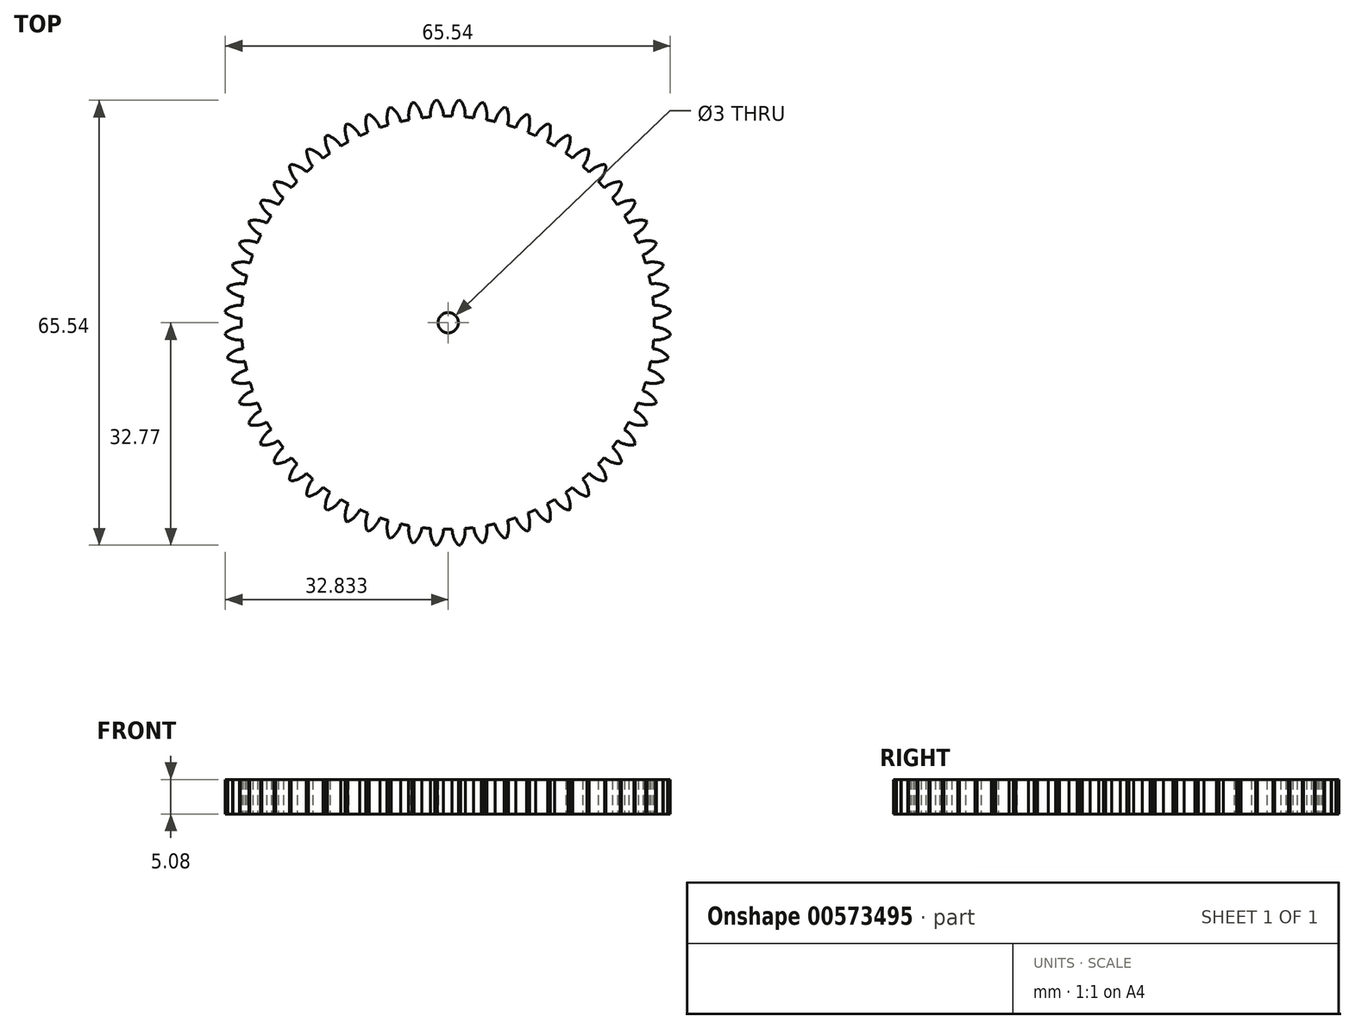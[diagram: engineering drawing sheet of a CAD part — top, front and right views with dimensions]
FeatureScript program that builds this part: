
annotation { "Feature Type Name" : "Feature", "Feature Type Description" : "" }
export const myFeature = defineFeature(function(context is Context, id is Id, definition is map)
    precondition{}
    {
        {
            var Q0;
            Q0=qCreatedBy(makeId("Top.planeOp"),FACE);
            var sketch = newSketch(context, id + "F0", { "sketchPlane" : qUnion([Q0])});
            skArc(sketch, "E0", {"start": v(-17.72, -27.6) * mm, "mid": v(-16.6, -26.98) * mm, "end": v(-15.76, -26.02) * mm});
            skLineSegment(sketch, "E1", {"start": v(-17.72, -27.6) * mm, "end": v(-18.01, -27.42) * mm});
            skArc(sketch, "E2", {"start": v(-17.36, -24.98) * mm, "mid": v(-17.9, -26.14) * mm, "end": v(-18.01, -27.42) * mm});
            skArc(sketch, "E3", {"start": v(-18.4, -24.23) * mm, "mid": v(-17.88, -24.6) * mm, "end": v(-17.36, -24.98) * mm});
            skArc(sketch, "E4.1.0", {"start": v(-14.74, -29.3) * mm, "mid": v(-13.69, -28.57) * mm, "end": v(-12.95, -27.52) * mm});
            skLineSegment(sketch, "E4.1.1", {"start": v(-14.74, -29.3) * mm, "end": v(-15.05, -29.15) * mm});
            skArc(sketch, "E4.1.2", {"start": v(-14.65, -26.66) * mm, "mid": v(-15.07, -27.87) * mm, "end": v(-15.05, -29.15) * mm});
            skArc(sketch, "E4.1.3", {"start": v(-15.76, -26.02) * mm, "mid": v(-15.2, -26.34) * mm, "end": v(-14.65, -26.66) * mm});
            skArc(sketch, "E4.2.0", {"start": v(-11.6, -30.69) * mm, "mid": v(-10.63, -29.85) * mm, "end": v(-10, -28.73) * mm});
            skLineSegment(sketch, "E4.2.1", {"start": v(-11.6, -30.69) * mm, "end": v(-11.92, -30.56) * mm});
            skArc(sketch, "E4.2.2", {"start": v(-11.79, -28.04) * mm, "mid": v(-12.07, -29.3) * mm, "end": v(-11.92, -30.56) * mm});
            skArc(sketch, "E4.2.3", {"start": v(-12.95, -27.52) * mm, "mid": v(-12.37, -27.79) * mm, "end": v(-11.79, -28.04) * mm});
            skArc(sketch, "E4.3.0", {"start": v(-8.32, -31.73) * mm, "mid": v(-7.45, -30.8) * mm, "end": v(-6.95, -29.61) * mm});
            skLineSegment(sketch, "E4.3.1", {"start": v(-8.32, -31.73) * mm, "end": v(-8.66, -31.64) * mm});
            skArc(sketch, "E4.3.2", {"start": v(-8.8, -29.12) * mm, "mid": v(-8.94, -30.4) * mm, "end": v(-8.66, -31.64) * mm});
            skArc(sketch, "E4.3.3", {"start": v(-10, -28.73) * mm, "mid": v(-9.4, -28.93) * mm, "end": v(-8.8, -29.12) * mm});
            skArc(sketch, "E4.4.0", {"start": v(-4.96, -32.43) * mm, "mid": v(-4.2, -31.4) * mm, "end": v(-3.81, -30.18) * mm});
            skLineSegment(sketch, "E4.4.1", {"start": v(-4.96, -32.43) * mm, "end": v(-5.3, -32.37) * mm});
            skArc(sketch, "E4.4.2", {"start": v(-5.7, -29.88) * mm, "mid": v(-5.72, -31.16) * mm, "end": v(-5.3, -32.37) * mm});
            skArc(sketch, "E4.4.3", {"start": v(-6.95, -29.61) * mm, "mid": v(-6.32, -29.75) * mm, "end": v(-5.7, -29.88) * mm});
            skArc(sketch, "E4.5.0", {"start": v(-1.55, -32.77) * mm, "mid": v(-0.88, -31.67) * mm, "end": v(-0.64, -30.41) * mm});
            skLineSegment(sketch, "E4.5.1", {"start": v(-1.55, -32.77) * mm, "end": v(-1.89, -32.75) * mm});
            skArc(sketch, "E4.5.2", {"start": v(-2.55, -30.31) * mm, "mid": v(-2.43, -31.59) * mm, "end": v(-1.89, -32.75) * mm});
            skArc(sketch, "E4.5.3", {"start": v(-3.81, -30.18) * mm, "mid": v(-3.18, -30.25) * mm, "end": v(-2.55, -30.31) * mm});
            skArc(sketch, "E4.6.0", {"start": v(1.89, -32.75) * mm, "mid": v(2.43, -31.59) * mm, "end": v(2.55, -30.31) * mm});
            skLineSegment(sketch, "E4.6.1", {"start": v(1.89, -32.75) * mm, "end": v(1.55, -32.77) * mm});
            skArc(sketch, "E4.6.2", {"start": v(0.64, -30.41) * mm, "mid": v(0.88, -31.67) * mm, "end": v(1.55, -32.77) * mm});
            skArc(sketch, "E4.6.3", {"start": v(-0.64, -30.41) * mm, "mid": v(0, -30.42) * mm, "end": v(0.64, -30.41) * mm});
            skArc(sketch, "E4.7.0", {"start": v(5.3, -32.37) * mm, "mid": v(5.72, -31.16) * mm, "end": v(5.7, -29.88) * mm});
            skLineSegment(sketch, "E4.7.1", {"start": v(5.3, -32.37) * mm, "end": v(4.96, -32.43) * mm});
            skArc(sketch, "E4.7.2", {"start": v(3.81, -30.18) * mm, "mid": v(4.2, -31.4) * mm, "end": v(4.96, -32.43) * mm});
            skArc(sketch, "E4.7.3", {"start": v(2.55, -30.31) * mm, "mid": v(3.18, -30.25) * mm, "end": v(3.81, -30.18) * mm});
            skArc(sketch, "E4.8.0", {"start": v(8.66, -31.64) * mm, "mid": v(8.94, -30.4) * mm, "end": v(8.8, -29.12) * mm});
            skLineSegment(sketch, "E4.8.1", {"start": v(8.66, -31.64) * mm, "end": v(8.32, -31.73) * mm});
            skArc(sketch, "E4.8.2", {"start": v(6.95, -29.61) * mm, "mid": v(7.45, -30.8) * mm, "end": v(8.32, -31.73) * mm});
            skArc(sketch, "E4.8.3", {"start": v(5.7, -29.88) * mm, "mid": v(6.32, -29.75) * mm, "end": v(6.95, -29.61) * mm});
            skArc(sketch, "E4.9.0", {"start": v(11.92, -30.56) * mm, "mid": v(12.07, -29.3) * mm, "end": v(11.79, -28.04) * mm});
            skLineSegment(sketch, "E4.9.1", {"start": v(11.92, -30.56) * mm, "end": v(11.6, -30.69) * mm});
            skArc(sketch, "E4.9.2", {"start": v(10, -28.73) * mm, "mid": v(10.63, -29.85) * mm, "end": v(11.6, -30.69) * mm});
            skArc(sketch, "E4.9.3", {"start": v(8.8, -29.12) * mm, "mid": v(9.4, -28.93) * mm, "end": v(10, -28.73) * mm});
            skArc(sketch, "E4.10.0", {"start": v(15.05, -29.15) * mm, "mid": v(15.07, -27.87) * mm, "end": v(14.65, -26.66) * mm});
            skLineSegment(sketch, "E4.10.1", {"start": v(15.05, -29.15) * mm, "end": v(14.74, -29.3) * mm});
            skArc(sketch, "E4.10.2", {"start": v(12.95, -27.52) * mm, "mid": v(13.69, -28.57) * mm, "end": v(14.74, -29.3) * mm});
            skArc(sketch, "E4.10.3", {"start": v(11.79, -28.04) * mm, "mid": v(12.37, -27.79) * mm, "end": v(12.95, -27.52) * mm});
            skArc(sketch, "E4.11.0", {"start": v(18.01, -27.42) * mm, "mid": v(17.9, -26.14) * mm, "end": v(17.36, -24.98) * mm});
            skLineSegment(sketch, "E4.11.1", {"start": v(18.01, -27.42) * mm, "end": v(17.72, -27.6) * mm});
            skArc(sketch, "E4.11.2", {"start": v(15.76, -26.02) * mm, "mid": v(16.6, -26.98) * mm, "end": v(17.72, -27.6) * mm});
            skArc(sketch, "E4.11.3", {"start": v(14.65, -26.66) * mm, "mid": v(15.2, -26.34) * mm, "end": v(15.76, -26.02) * mm});
            skArc(sketch, "E4.12.0", {"start": v(20.78, -25.39) * mm, "mid": v(20.53, -24.13) * mm, "end": v(19.88, -23.03) * mm});
            skLineSegment(sketch, "E4.12.1", {"start": v(20.78, -25.39) * mm, "end": v(20.51, -25.6) * mm});
            skArc(sketch, "E4.12.2", {"start": v(18.4, -24.23) * mm, "mid": v(19.33, -25.1) * mm, "end": v(20.51, -25.6) * mm});
            skArc(sketch, "E4.12.3", {"start": v(17.36, -24.98) * mm, "mid": v(17.88, -24.6) * mm, "end": v(18.4, -24.23) * mm});
            skArc(sketch, "E4.13.0", {"start": v(23.32, -23.07) * mm, "mid": v(22.94, -21.85) * mm, "end": v(22.17, -20.82) * mm});
            skLineSegment(sketch, "E4.13.1", {"start": v(23.32, -23.07) * mm, "end": v(23.07, -23.32) * mm});
            skArc(sketch, "E4.13.2", {"start": v(20.82, -22.17) * mm, "mid": v(21.85, -22.94) * mm, "end": v(23.07, -23.32) * mm});
            skArc(sketch, "E4.13.3", {"start": v(19.88, -23.03) * mm, "mid": v(20.35, -22.6) * mm, "end": v(20.82, -22.17) * mm});
            skArc(sketch, "E4.14.0", {"start": v(25.6, -20.51) * mm, "mid": v(25.1, -19.33) * mm, "end": v(24.23, -18.4) * mm});
            skLineSegment(sketch, "E4.14.1", {"start": v(25.6, -20.51) * mm, "end": v(25.39, -20.78) * mm});
            skArc(sketch, "E4.14.2", {"start": v(23.03, -19.88) * mm, "mid": v(24.13, -20.53) * mm, "end": v(25.39, -20.78) * mm});
            skArc(sketch, "E4.14.3", {"start": v(22.17, -20.82) * mm, "mid": v(22.6, -20.35) * mm, "end": v(23.03, -19.88) * mm});
            skArc(sketch, "E4.15.0", {"start": v(27.6, -17.72) * mm, "mid": v(26.98, -16.6) * mm, "end": v(26.02, -15.76) * mm});
            skLineSegment(sketch, "E4.15.1", {"start": v(27.6, -17.72) * mm, "end": v(27.42, -18.01) * mm});
            skArc(sketch, "E4.15.2", {"start": v(24.98, -17.36) * mm, "mid": v(26.14, -17.9) * mm, "end": v(27.42, -18.01) * mm});
            skArc(sketch, "E4.15.3", {"start": v(24.23, -18.4) * mm, "mid": v(24.6, -17.88) * mm, "end": v(24.98, -17.36) * mm});
            skArc(sketch, "E4.16.0", {"start": v(29.3, -14.74) * mm, "mid": v(28.57, -13.69) * mm, "end": v(27.52, -12.95) * mm});
            skLineSegment(sketch, "E4.16.1", {"start": v(29.3, -14.74) * mm, "end": v(29.15, -15.05) * mm});
            skArc(sketch, "E4.16.2", {"start": v(26.66, -14.65) * mm, "mid": v(27.87, -15.07) * mm, "end": v(29.15, -15.05) * mm});
            skArc(sketch, "E4.16.3", {"start": v(26.02, -15.76) * mm, "mid": v(26.34, -15.2) * mm, "end": v(26.66, -14.65) * mm});
            skArc(sketch, "E4.17.0", {"start": v(30.69, -11.6) * mm, "mid": v(29.85, -10.63) * mm, "end": v(28.73, -10) * mm});
            skLineSegment(sketch, "E4.17.1", {"start": v(30.69, -11.6) * mm, "end": v(30.56, -11.92) * mm});
            skArc(sketch, "E4.17.2", {"start": v(28.04, -11.79) * mm, "mid": v(29.3, -12.07) * mm, "end": v(30.56, -11.92) * mm});
            skArc(sketch, "E4.17.3", {"start": v(27.52, -12.95) * mm, "mid": v(27.79, -12.37) * mm, "end": v(28.04, -11.79) * mm});
            skArc(sketch, "E4.18.0", {"start": v(31.73, -8.32) * mm, "mid": v(30.8, -7.45) * mm, "end": v(29.61, -6.95) * mm});
            skLineSegment(sketch, "E4.18.1", {"start": v(31.73, -8.32) * mm, "end": v(31.64, -8.66) * mm});
            skArc(sketch, "E4.18.2", {"start": v(29.12, -8.8) * mm, "mid": v(30.4, -8.94) * mm, "end": v(31.64, -8.66) * mm});
            skArc(sketch, "E4.18.3", {"start": v(28.73, -10) * mm, "mid": v(28.93, -9.4) * mm, "end": v(29.12, -8.8) * mm});
            skArc(sketch, "E4.19.0", {"start": v(32.43, -4.96) * mm, "mid": v(31.4, -4.2) * mm, "end": v(30.18, -3.81) * mm});
            skLineSegment(sketch, "E4.19.1", {"start": v(32.43, -4.96) * mm, "end": v(32.37, -5.3) * mm});
            skArc(sketch, "E4.19.2", {"start": v(29.88, -5.7) * mm, "mid": v(31.16, -5.72) * mm, "end": v(32.37, -5.3) * mm});
            skArc(sketch, "E4.19.3", {"start": v(29.61, -6.95) * mm, "mid": v(29.75, -6.32) * mm, "end": v(29.88, -5.7) * mm});
            skArc(sketch, "E4.20.0", {"start": v(32.77, -1.55) * mm, "mid": v(31.67, -0.88) * mm, "end": v(30.41, -0.64) * mm});
            skLineSegment(sketch, "E4.20.1", {"start": v(32.77, -1.55) * mm, "end": v(32.75, -1.89) * mm});
            skArc(sketch, "E4.20.2", {"start": v(30.31, -2.55) * mm, "mid": v(31.59, -2.43) * mm, "end": v(32.75, -1.89) * mm});
            skArc(sketch, "E4.20.3", {"start": v(30.18, -3.81) * mm, "mid": v(30.25, -3.18) * mm, "end": v(30.31, -2.55) * mm});
            skArc(sketch, "E4.21.0", {"start": v(32.75, 1.89) * mm, "mid": v(31.59, 2.43) * mm, "end": v(30.31, 2.55) * mm});
            skLineSegment(sketch, "E4.21.1", {"start": v(32.75, 1.89) * mm, "end": v(32.77, 1.55) * mm});
            skArc(sketch, "E4.21.2", {"start": v(30.41, 0.64) * mm, "mid": v(31.67, 0.88) * mm, "end": v(32.77, 1.55) * mm});
            skArc(sketch, "E4.21.3", {"start": v(30.41, -0.64) * mm, "mid": v(30.42, 0) * mm, "end": v(30.41, 0.64) * mm});
            skArc(sketch, "E4.22.0", {"start": v(32.37, 5.3) * mm, "mid": v(31.16, 5.72) * mm, "end": v(29.88, 5.7) * mm});
            skLineSegment(sketch, "E4.22.1", {"start": v(32.37, 5.3) * mm, "end": v(32.43, 4.96) * mm});
            skArc(sketch, "E4.22.2", {"start": v(30.18, 3.81) * mm, "mid": v(31.4, 4.2) * mm, "end": v(32.43, 4.96) * mm});
            skArc(sketch, "E4.22.3", {"start": v(30.31, 2.55) * mm, "mid": v(30.25, 3.18) * mm, "end": v(30.18, 3.81) * mm});
            skArc(sketch, "E4.23.0", {"start": v(31.64, 8.66) * mm, "mid": v(30.4, 8.94) * mm, "end": v(29.12, 8.8) * mm});
            skLineSegment(sketch, "E4.23.1", {"start": v(31.64, 8.66) * mm, "end": v(31.73, 8.32) * mm});
            skArc(sketch, "E4.23.2", {"start": v(29.61, 6.95) * mm, "mid": v(30.8, 7.45) * mm, "end": v(31.73, 8.32) * mm});
            skArc(sketch, "E4.23.3", {"start": v(29.88, 5.7) * mm, "mid": v(29.75, 6.32) * mm, "end": v(29.61, 6.95) * mm});
            skArc(sketch, "E4.24.0", {"start": v(30.56, 11.92) * mm, "mid": v(29.3, 12.07) * mm, "end": v(28.04, 11.79) * mm});
            skLineSegment(sketch, "E4.24.1", {"start": v(30.56, 11.92) * mm, "end": v(30.69, 11.6) * mm});
            skArc(sketch, "E4.24.2", {"start": v(28.73, 10) * mm, "mid": v(29.85, 10.63) * mm, "end": v(30.69, 11.6) * mm});
            skArc(sketch, "E4.24.3", {"start": v(29.12, 8.8) * mm, "mid": v(28.93, 9.4) * mm, "end": v(28.73, 10) * mm});
            skArc(sketch, "E4.25.0", {"start": v(29.15, 15.05) * mm, "mid": v(27.87, 15.07) * mm, "end": v(26.66, 14.65) * mm});
            skLineSegment(sketch, "E4.25.1", {"start": v(29.15, 15.05) * mm, "end": v(29.3, 14.74) * mm});
            skArc(sketch, "E4.25.2", {"start": v(27.52, 12.95) * mm, "mid": v(28.57, 13.69) * mm, "end": v(29.3, 14.74) * mm});
            skArc(sketch, "E4.25.3", {"start": v(28.04, 11.79) * mm, "mid": v(27.79, 12.37) * mm, "end": v(27.52, 12.95) * mm});
            skArc(sketch, "E4.26.0", {"start": v(27.42, 18.01) * mm, "mid": v(26.14, 17.9) * mm, "end": v(24.98, 17.36) * mm});
            skLineSegment(sketch, "E4.26.1", {"start": v(27.42, 18.01) * mm, "end": v(27.6, 17.72) * mm});
            skArc(sketch, "E4.26.2", {"start": v(26.02, 15.76) * mm, "mid": v(26.98, 16.6) * mm, "end": v(27.6, 17.72) * mm});
            skArc(sketch, "E4.26.3", {"start": v(26.66, 14.65) * mm, "mid": v(26.34, 15.2) * mm, "end": v(26.02, 15.76) * mm});
            skArc(sketch, "E4.27.0", {"start": v(25.39, 20.78) * mm, "mid": v(24.13, 20.53) * mm, "end": v(23.03, 19.88) * mm});
            skLineSegment(sketch, "E4.27.1", {"start": v(25.39, 20.78) * mm, "end": v(25.6, 20.51) * mm});
            skArc(sketch, "E4.27.2", {"start": v(24.23, 18.4) * mm, "mid": v(25.1, 19.33) * mm, "end": v(25.6, 20.51) * mm});
            skArc(sketch, "E4.27.3", {"start": v(24.98, 17.36) * mm, "mid": v(24.6, 17.88) * mm, "end": v(24.23, 18.4) * mm});
            skArc(sketch, "E4.28.0", {"start": v(23.07, 23.32) * mm, "mid": v(21.85, 22.94) * mm, "end": v(20.82, 22.17) * mm});
            skLineSegment(sketch, "E4.28.1", {"start": v(23.07, 23.32) * mm, "end": v(23.32, 23.07) * mm});
            skArc(sketch, "E4.28.2", {"start": v(22.17, 20.82) * mm, "mid": v(22.94, 21.85) * mm, "end": v(23.32, 23.07) * mm});
            skArc(sketch, "E4.28.3", {"start": v(23.03, 19.88) * mm, "mid": v(22.6, 20.35) * mm, "end": v(22.17, 20.82) * mm});
            skArc(sketch, "E4.29.0", {"start": v(20.51, 25.6) * mm, "mid": v(19.33, 25.1) * mm, "end": v(18.4, 24.23) * mm});
            skLineSegment(sketch, "E4.29.1", {"start": v(20.51, 25.6) * mm, "end": v(20.78, 25.39) * mm});
            skArc(sketch, "E4.29.2", {"start": v(19.88, 23.03) * mm, "mid": v(20.53, 24.13) * mm, "end": v(20.78, 25.39) * mm});
            skArc(sketch, "E4.29.3", {"start": v(20.82, 22.17) * mm, "mid": v(20.35, 22.6) * mm, "end": v(19.88, 23.03) * mm});
            skArc(sketch, "E4.30.0", {"start": v(17.72, 27.6) * mm, "mid": v(16.6, 26.98) * mm, "end": v(15.76, 26.02) * mm});
            skLineSegment(sketch, "E4.30.1", {"start": v(17.72, 27.6) * mm, "end": v(18.01, 27.42) * mm});
            skArc(sketch, "E4.30.2", {"start": v(17.36, 24.98) * mm, "mid": v(17.9, 26.14) * mm, "end": v(18.01, 27.42) * mm});
            skArc(sketch, "E4.30.3", {"start": v(18.4, 24.23) * mm, "mid": v(17.88, 24.6) * mm, "end": v(17.36, 24.98) * mm});
            skArc(sketch, "E4.31.0", {"start": v(14.74, 29.3) * mm, "mid": v(13.69, 28.57) * mm, "end": v(12.95, 27.52) * mm});
            skLineSegment(sketch, "E4.31.1", {"start": v(14.74, 29.3) * mm, "end": v(15.05, 29.15) * mm});
            skArc(sketch, "E4.31.2", {"start": v(14.65, 26.66) * mm, "mid": v(15.07, 27.87) * mm, "end": v(15.05, 29.15) * mm});
            skArc(sketch, "E4.31.3", {"start": v(15.76, 26.02) * mm, "mid": v(15.2, 26.34) * mm, "end": v(14.65, 26.66) * mm});
            skArc(sketch, "E4.32.0", {"start": v(11.6, 30.69) * mm, "mid": v(10.63, 29.85) * mm, "end": v(10, 28.73) * mm});
            skLineSegment(sketch, "E4.32.1", {"start": v(11.6, 30.69) * mm, "end": v(11.92, 30.56) * mm});
            skArc(sketch, "E4.32.2", {"start": v(11.79, 28.04) * mm, "mid": v(12.07, 29.3) * mm, "end": v(11.92, 30.56) * mm});
            skArc(sketch, "E4.32.3", {"start": v(12.95, 27.52) * mm, "mid": v(12.37, 27.79) * mm, "end": v(11.79, 28.04) * mm});
            skArc(sketch, "E4.33.0", {"start": v(8.32, 31.73) * mm, "mid": v(7.45, 30.8) * mm, "end": v(6.95, 29.61) * mm});
            skLineSegment(sketch, "E4.33.1", {"start": v(8.32, 31.73) * mm, "end": v(8.66, 31.64) * mm});
            skArc(sketch, "E4.33.2", {"start": v(8.8, 29.12) * mm, "mid": v(8.94, 30.4) * mm, "end": v(8.66, 31.64) * mm});
            skArc(sketch, "E4.33.3", {"start": v(10, 28.73) * mm, "mid": v(9.4, 28.93) * mm, "end": v(8.8, 29.12) * mm});
            skArc(sketch, "E4.34.0", {"start": v(4.96, 32.43) * mm, "mid": v(4.2, 31.4) * mm, "end": v(3.81, 30.18) * mm});
            skLineSegment(sketch, "E4.34.1", {"start": v(4.96, 32.43) * mm, "end": v(5.3, 32.37) * mm});
            skArc(sketch, "E4.34.2", {"start": v(5.7, 29.88) * mm, "mid": v(5.72, 31.16) * mm, "end": v(5.3, 32.37) * mm});
            skArc(sketch, "E4.34.3", {"start": v(6.95, 29.61) * mm, "mid": v(6.32, 29.75) * mm, "end": v(5.7, 29.88) * mm});
            skArc(sketch, "E4.35.0", {"start": v(1.55, 32.77) * mm, "mid": v(0.88, 31.67) * mm, "end": v(0.64, 30.41) * mm});
            skLineSegment(sketch, "E4.35.1", {"start": v(1.55, 32.77) * mm, "end": v(1.89, 32.75) * mm});
            skArc(sketch, "E4.35.2", {"start": v(2.55, 30.31) * mm, "mid": v(2.43, 31.59) * mm, "end": v(1.89, 32.75) * mm});
            skArc(sketch, "E4.35.3", {"start": v(3.81, 30.18) * mm, "mid": v(3.18, 30.25) * mm, "end": v(2.55, 30.31) * mm});
            skArc(sketch, "E4.36.0", {"start": v(-1.89, 32.75) * mm, "mid": v(-2.43, 31.59) * mm, "end": v(-2.55, 30.31) * mm});
            skLineSegment(sketch, "E4.36.1", {"start": v(-1.89, 32.75) * mm, "end": v(-1.55, 32.77) * mm});
            skArc(sketch, "E4.36.2", {"start": v(-0.64, 30.41) * mm, "mid": v(-0.88, 31.67) * mm, "end": v(-1.55, 32.77) * mm});
            skArc(sketch, "E4.36.3", {"start": v(0.64, 30.41) * mm, "mid": v(0, 30.42) * mm, "end": v(-0.64, 30.41) * mm});
            skArc(sketch, "E4.37.0", {"start": v(-5.3, 32.37) * mm, "mid": v(-5.72, 31.16) * mm, "end": v(-5.7, 29.88) * mm});
            skLineSegment(sketch, "E4.37.1", {"start": v(-5.3, 32.37) * mm, "end": v(-4.96, 32.43) * mm});
            skArc(sketch, "E4.37.2", {"start": v(-3.81, 30.18) * mm, "mid": v(-4.2, 31.4) * mm, "end": v(-4.96, 32.43) * mm});
            skArc(sketch, "E4.37.3", {"start": v(-2.55, 30.31) * mm, "mid": v(-3.18, 30.25) * mm, "end": v(-3.81, 30.18) * mm});
            skArc(sketch, "E4.38.0", {"start": v(-8.66, 31.64) * mm, "mid": v(-8.94, 30.4) * mm, "end": v(-8.8, 29.12) * mm});
            skLineSegment(sketch, "E4.38.1", {"start": v(-8.66, 31.64) * mm, "end": v(-8.32, 31.73) * mm});
            skArc(sketch, "E4.38.2", {"start": v(-6.95, 29.61) * mm, "mid": v(-7.45, 30.8) * mm, "end": v(-8.32, 31.73) * mm});
            skArc(sketch, "E4.38.3", {"start": v(-5.7, 29.88) * mm, "mid": v(-6.32, 29.75) * mm, "end": v(-6.95, 29.61) * mm});
            skArc(sketch, "E4.39.0", {"start": v(-11.92, 30.56) * mm, "mid": v(-12.07, 29.3) * mm, "end": v(-11.79, 28.04) * mm});
            skLineSegment(sketch, "E4.39.1", {"start": v(-11.92, 30.56) * mm, "end": v(-11.6, 30.69) * mm});
            skArc(sketch, "E4.39.2", {"start": v(-10, 28.73) * mm, "mid": v(-10.63, 29.85) * mm, "end": v(-11.6, 30.69) * mm});
            skArc(sketch, "E4.39.3", {"start": v(-8.8, 29.12) * mm, "mid": v(-9.4, 28.93) * mm, "end": v(-10, 28.73) * mm});
            skArc(sketch, "E4.40.0", {"start": v(-15.05, 29.15) * mm, "mid": v(-15.07, 27.87) * mm, "end": v(-14.65, 26.66) * mm});
            skLineSegment(sketch, "E4.40.1", {"start": v(-15.05, 29.15) * mm, "end": v(-14.74, 29.3) * mm});
            skArc(sketch, "E4.40.2", {"start": v(-12.95, 27.52) * mm, "mid": v(-13.69, 28.57) * mm, "end": v(-14.74, 29.3) * mm});
            skArc(sketch, "E4.40.3", {"start": v(-11.79, 28.04) * mm, "mid": v(-12.37, 27.79) * mm, "end": v(-12.95, 27.52) * mm});
            skArc(sketch, "E4.41.0", {"start": v(-18.01, 27.42) * mm, "mid": v(-17.9, 26.14) * mm, "end": v(-17.36, 24.98) * mm});
            skLineSegment(sketch, "E4.41.1", {"start": v(-18.01, 27.42) * mm, "end": v(-17.72, 27.6) * mm});
            skArc(sketch, "E4.41.2", {"start": v(-15.76, 26.02) * mm, "mid": v(-16.6, 26.98) * mm, "end": v(-17.72, 27.6) * mm});
            skArc(sketch, "E4.41.3", {"start": v(-14.65, 26.66) * mm, "mid": v(-15.2, 26.34) * mm, "end": v(-15.76, 26.02) * mm});
            skArc(sketch, "E4.42.0", {"start": v(-20.78, 25.39) * mm, "mid": v(-20.53, 24.13) * mm, "end": v(-19.88, 23.03) * mm});
            skLineSegment(sketch, "E4.42.1", {"start": v(-20.78, 25.39) * mm, "end": v(-20.51, 25.6) * mm});
            skArc(sketch, "E4.42.2", {"start": v(-18.4, 24.23) * mm, "mid": v(-19.33, 25.1) * mm, "end": v(-20.51, 25.6) * mm});
            skArc(sketch, "E4.42.3", {"start": v(-17.36, 24.98) * mm, "mid": v(-17.88, 24.6) * mm, "end": v(-18.4, 24.23) * mm});
            skArc(sketch, "E4.43.0", {"start": v(-23.32, 23.07) * mm, "mid": v(-22.94, 21.85) * mm, "end": v(-22.17, 20.82) * mm});
            skLineSegment(sketch, "E4.43.1", {"start": v(-23.32, 23.07) * mm, "end": v(-23.07, 23.32) * mm});
            skArc(sketch, "E4.43.2", {"start": v(-20.82, 22.17) * mm, "mid": v(-21.85, 22.94) * mm, "end": v(-23.07, 23.32) * mm});
            skArc(sketch, "E4.43.3", {"start": v(-19.88, 23.03) * mm, "mid": v(-20.35, 22.6) * mm, "end": v(-20.82, 22.17) * mm});
            skArc(sketch, "E4.44.0", {"start": v(-25.6, 20.51) * mm, "mid": v(-25.1, 19.33) * mm, "end": v(-24.23, 18.4) * mm});
            skLineSegment(sketch, "E4.44.1", {"start": v(-25.6, 20.51) * mm, "end": v(-25.39, 20.78) * mm});
            skArc(sketch, "E4.44.2", {"start": v(-23.03, 19.88) * mm, "mid": v(-24.13, 20.53) * mm, "end": v(-25.39, 20.78) * mm});
            skArc(sketch, "E4.44.3", {"start": v(-22.17, 20.82) * mm, "mid": v(-22.6, 20.35) * mm, "end": v(-23.03, 19.88) * mm});
            skArc(sketch, "E4.45.0", {"start": v(-27.6, 17.72) * mm, "mid": v(-26.98, 16.6) * mm, "end": v(-26.02, 15.76) * mm});
            skLineSegment(sketch, "E4.45.1", {"start": v(-27.6, 17.72) * mm, "end": v(-27.42, 18.01) * mm});
            skArc(sketch, "E4.45.2", {"start": v(-24.98, 17.36) * mm, "mid": v(-26.14, 17.9) * mm, "end": v(-27.42, 18.01) * mm});
            skArc(sketch, "E4.45.3", {"start": v(-24.23, 18.4) * mm, "mid": v(-24.6, 17.88) * mm, "end": v(-24.98, 17.36) * mm});
            skArc(sketch, "E4.46.0", {"start": v(-29.3, 14.74) * mm, "mid": v(-28.57, 13.69) * mm, "end": v(-27.52, 12.95) * mm});
            skLineSegment(sketch, "E4.46.1", {"start": v(-29.3, 14.74) * mm, "end": v(-29.15, 15.05) * mm});
            skArc(sketch, "E4.46.2", {"start": v(-26.66, 14.65) * mm, "mid": v(-27.87, 15.07) * mm, "end": v(-29.15, 15.05) * mm});
            skArc(sketch, "E4.46.3", {"start": v(-26.02, 15.76) * mm, "mid": v(-26.34, 15.2) * mm, "end": v(-26.66, 14.65) * mm});
            skArc(sketch, "E4.47.0", {"start": v(-30.69, 11.6) * mm, "mid": v(-29.85, 10.63) * mm, "end": v(-28.73, 10) * mm});
            skLineSegment(sketch, "E4.47.1", {"start": v(-30.69, 11.6) * mm, "end": v(-30.56, 11.92) * mm});
            skArc(sketch, "E4.47.2", {"start": v(-28.04, 11.79) * mm, "mid": v(-29.3, 12.07) * mm, "end": v(-30.56, 11.92) * mm});
            skArc(sketch, "E4.47.3", {"start": v(-27.52, 12.95) * mm, "mid": v(-27.79, 12.37) * mm, "end": v(-28.04, 11.79) * mm});
            skArc(sketch, "E4.48.0", {"start": v(-31.73, 8.32) * mm, "mid": v(-30.8, 7.45) * mm, "end": v(-29.61, 6.95) * mm});
            skLineSegment(sketch, "E4.48.1", {"start": v(-31.73, 8.32) * mm, "end": v(-31.64, 8.66) * mm});
            skArc(sketch, "E4.48.2", {"start": v(-29.12, 8.8) * mm, "mid": v(-30.4, 8.94) * mm, "end": v(-31.64, 8.66) * mm});
            skArc(sketch, "E4.48.3", {"start": v(-28.73, 10) * mm, "mid": v(-28.93, 9.4) * mm, "end": v(-29.12, 8.8) * mm});
            skArc(sketch, "E4.49.0", {"start": v(-32.43, 4.96) * mm, "mid": v(-31.4, 4.2) * mm, "end": v(-30.18, 3.81) * mm});
            skLineSegment(sketch, "E4.49.1", {"start": v(-32.43, 4.96) * mm, "end": v(-32.37, 5.3) * mm});
            skArc(sketch, "E4.49.2", {"start": v(-29.88, 5.7) * mm, "mid": v(-31.16, 5.72) * mm, "end": v(-32.37, 5.3) * mm});
            skArc(sketch, "E4.49.3", {"start": v(-29.61, 6.95) * mm, "mid": v(-29.75, 6.32) * mm, "end": v(-29.88, 5.7) * mm});
            skArc(sketch, "E4.50.0", {"start": v(-32.77, 1.55) * mm, "mid": v(-31.67, 0.88) * mm, "end": v(-30.41, 0.64) * mm});
            skLineSegment(sketch, "E4.50.1", {"start": v(-32.77, 1.55) * mm, "end": v(-32.75, 1.89) * mm});
            skArc(sketch, "E4.50.2", {"start": v(-30.31, 2.55) * mm, "mid": v(-31.59, 2.43) * mm, "end": v(-32.75, 1.89) * mm});
            skArc(sketch, "E4.50.3", {"start": v(-30.18, 3.81) * mm, "mid": v(-30.25, 3.18) * mm, "end": v(-30.31, 2.55) * mm});
            skArc(sketch, "E4.51.0", {"start": v(-32.75, -1.89) * mm, "mid": v(-31.59, -2.43) * mm, "end": v(-30.31, -2.55) * mm});
            skLineSegment(sketch, "E4.51.1", {"start": v(-32.75, -1.89) * mm, "end": v(-32.77, -1.55) * mm});
            skArc(sketch, "E4.51.2", {"start": v(-30.41, -0.64) * mm, "mid": v(-31.67, -0.88) * mm, "end": v(-32.77, -1.55) * mm});
            skArc(sketch, "E4.51.3", {"start": v(-30.41, 0.64) * mm, "mid": v(-30.42, 0) * mm, "end": v(-30.41, -0.64) * mm});
            skArc(sketch, "E4.52.0", {"start": v(-32.37, -5.3) * mm, "mid": v(-31.16, -5.72) * mm, "end": v(-29.88, -5.7) * mm});
            skLineSegment(sketch, "E4.52.1", {"start": v(-32.37, -5.3) * mm, "end": v(-32.43, -4.96) * mm});
            skArc(sketch, "E4.52.2", {"start": v(-30.18, -3.81) * mm, "mid": v(-31.4, -4.2) * mm, "end": v(-32.43, -4.96) * mm});
            skArc(sketch, "E4.52.3", {"start": v(-30.31, -2.55) * mm, "mid": v(-30.25, -3.18) * mm, "end": v(-30.18, -3.81) * mm});
            skArc(sketch, "E4.53.0", {"start": v(-31.64, -8.66) * mm, "mid": v(-30.4, -8.94) * mm, "end": v(-29.12, -8.8) * mm});
            skLineSegment(sketch, "E4.53.1", {"start": v(-31.64, -8.66) * mm, "end": v(-31.73, -8.32) * mm});
            skArc(sketch, "E4.53.2", {"start": v(-29.61, -6.95) * mm, "mid": v(-30.8, -7.45) * mm, "end": v(-31.73, -8.32) * mm});
            skArc(sketch, "E4.53.3", {"start": v(-29.88, -5.7) * mm, "mid": v(-29.75, -6.32) * mm, "end": v(-29.61, -6.95) * mm});
            skArc(sketch, "E4.54.0", {"start": v(-30.56, -11.92) * mm, "mid": v(-29.3, -12.07) * mm, "end": v(-28.04, -11.79) * mm});
            skLineSegment(sketch, "E4.54.1", {"start": v(-30.56, -11.92) * mm, "end": v(-30.69, -11.6) * mm});
            skArc(sketch, "E4.54.2", {"start": v(-28.73, -10) * mm, "mid": v(-29.85, -10.63) * mm, "end": v(-30.69, -11.6) * mm});
            skArc(sketch, "E4.54.3", {"start": v(-29.12, -8.8) * mm, "mid": v(-28.93, -9.4) * mm, "end": v(-28.73, -10) * mm});
            skArc(sketch, "E4.55.0", {"start": v(-29.15, -15.05) * mm, "mid": v(-27.87, -15.07) * mm, "end": v(-26.66, -14.65) * mm});
            skLineSegment(sketch, "E4.55.1", {"start": v(-29.15, -15.05) * mm, "end": v(-29.3, -14.74) * mm});
            skArc(sketch, "E4.55.2", {"start": v(-27.52, -12.95) * mm, "mid": v(-28.57, -13.69) * mm, "end": v(-29.3, -14.74) * mm});
            skArc(sketch, "E4.55.3", {"start": v(-28.04, -11.79) * mm, "mid": v(-27.79, -12.37) * mm, "end": v(-27.52, -12.95) * mm});
            skArc(sketch, "E4.56.0", {"start": v(-27.42, -18.01) * mm, "mid": v(-26.14, -17.9) * mm, "end": v(-24.98, -17.36) * mm});
            skLineSegment(sketch, "E4.56.1", {"start": v(-27.42, -18.01) * mm, "end": v(-27.6, -17.72) * mm});
            skArc(sketch, "E4.56.2", {"start": v(-26.02, -15.76) * mm, "mid": v(-26.98, -16.6) * mm, "end": v(-27.6, -17.72) * mm});
            skArc(sketch, "E4.56.3", {"start": v(-26.66, -14.65) * mm, "mid": v(-26.34, -15.2) * mm, "end": v(-26.02, -15.76) * mm});
            skArc(sketch, "E4.57.0", {"start": v(-25.39, -20.78) * mm, "mid": v(-24.13, -20.53) * mm, "end": v(-23.03, -19.88) * mm});
            skLineSegment(sketch, "E4.57.1", {"start": v(-25.39, -20.78) * mm, "end": v(-25.6, -20.51) * mm});
            skArc(sketch, "E4.57.2", {"start": v(-24.23, -18.4) * mm, "mid": v(-25.1, -19.33) * mm, "end": v(-25.6, -20.51) * mm});
            skArc(sketch, "E4.57.3", {"start": v(-24.98, -17.36) * mm, "mid": v(-24.6, -17.88) * mm, "end": v(-24.23, -18.4) * mm});
            skArc(sketch, "E4.58.0", {"start": v(-23.07, -23.32) * mm, "mid": v(-21.85, -22.94) * mm, "end": v(-20.82, -22.17) * mm});
            skLineSegment(sketch, "E4.58.1", {"start": v(-23.07, -23.32) * mm, "end": v(-23.32, -23.07) * mm});
            skArc(sketch, "E4.58.2", {"start": v(-22.17, -20.82) * mm, "mid": v(-22.94, -21.85) * mm, "end": v(-23.32, -23.07) * mm});
            skArc(sketch, "E4.58.3", {"start": v(-23.03, -19.88) * mm, "mid": v(-22.6, -20.35) * mm, "end": v(-22.17, -20.82) * mm});
            skArc(sketch, "E4.59.0", {"start": v(-20.51, -25.6) * mm, "mid": v(-19.33, -25.1) * mm, "end": v(-18.4, -24.23) * mm});
            skLineSegment(sketch, "E4.59.1", {"start": v(-20.51, -25.6) * mm, "end": v(-20.78, -25.39) * mm});
            skArc(sketch, "E4.59.2", {"start": v(-19.88, -23.03) * mm, "mid": v(-20.53, -24.13) * mm, "end": v(-20.78, -25.39) * mm});
            skArc(sketch, "E4.59.3", {"start": v(-20.82, -22.17) * mm, "mid": v(-20.35, -22.6) * mm, "end": v(-19.88, -23.03) * mm});
            skPoint(sketch, "E4.center", {"position": v(0, 0) * mm});
            skCircle(sketch, "E5", {"center": v(0.06, 0) * mm, "radius": 1.5 * mm});
            skSolve(sketch);
        }
        {
            var Q0;
            Q0=makeQuery(id+"F0.imprint","IMPRINT",FACE,{"disambiguationData":[TD([[makeQuery(id+"F0.imprint","IMPRINT",EDGE,{"derivedFrom":sQuery(id+"F0.wireOp",EDGE,"E0")}),1.0]])]});
            extrude(context, id + "F1", {"entities" : qUnion([Q0]), "depth" : 5.08 * mm, "offsetDistance" : 25 * mm});
        }
    });
